# Revit family: LD6LED4P
name_source: partatom
category: Lighting Fixtures
revit_build: Autodesk Revit Architecture 2012 (Build: 20110309_2315(x64)
units: mm (PartAtom-declared; Revit-internal decimal feet)

## types (4) — shared parameters
Backbox = Steel
Color Filter = 16777215
Default Elevation = 48.000"
Description = 6' LED Pendant Mount Cylinder
Dimming Lamp Color Temperature Shift = <None>
Emit from Line Length = 24.000"
Glass = Glass
Lamp = 1
Manufacturer = prescolite
Manufacturer Fax = 864-678-1415
Model = LD6LED4P
Product Documentation Link = http://www.prescolite.com
Product Page URL = http://www.prescolite.com
Tilt Angle = -90.00°
URL = http://www.prescolite.com
Voltage = 120 V
Wattage Comments = 14-999W

## per-type parameters (varying)
| type | Photometric Web File |
| LD6LED4 Nichia LED Array 3500 Kelvin with 45° flood distribution | 2925.IES |
| LD6LED4 Nichia LED Array 3500 Kelvin with 35° flood distribution | 2924.IES |
| LD6LED4 Nichia LED Array 3500 Kelvin with 25° medium distribution | 2923.IES |
| LD6LED4 Nichia LED Array 3500 Kelvin with 18° spot distribution | 2922.IES |

## geometry (parser evidence)
native form markers: Sweep x1
no freeform markers — native parametric forms only
